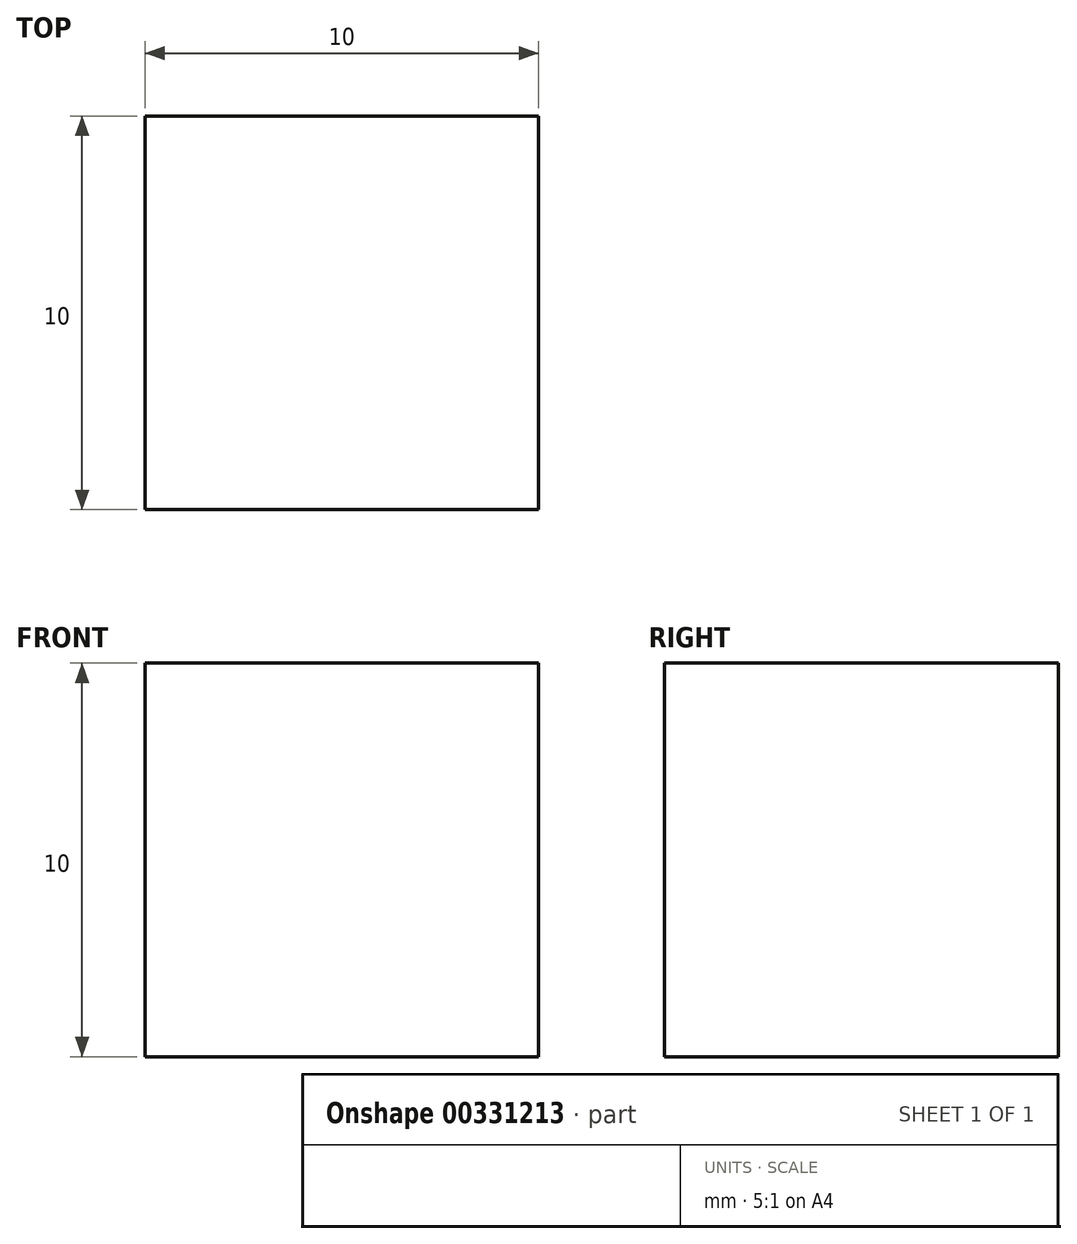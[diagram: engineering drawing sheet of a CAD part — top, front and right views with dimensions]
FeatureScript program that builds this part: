
annotation { "Feature Type Name" : "Feature", "Feature Type Description" : "" }
export const myFeature = defineFeature(function(context is Context, id is Id, definition is map)
    precondition{}
    {
        {
            var Q0;
            Q0=qCreatedBy(makeId("Front.planeOp"),FACE);
            var sketch = newSketch(context, id + "F0", { "sketchPlane" : qUnion([Q0])});
            skLineSegment(sketch, "E0.bottom", {"start": v(5, -5) * mm, "end": v(-5, -5) * mm});
            skLineSegment(sketch, "E0.top", {"start": v(5, 5) * mm, "end": v(-5, 5) * mm});
            skLineSegment(sketch, "E0.left", {"start": v(5, -5) * mm, "end": v(5, 5) * mm});
            skLineSegment(sketch, "E0.right", {"start": v(-5, -5) * mm, "end": v(-5, 5) * mm});
            skPoint(sketch, "E0.middle", {"position": v(0, 0) * mm});
            skSolve(sketch);
        }
        {
            var Q0;
            Q0 = qSketchRegion(id + "F0", true);
            extrude(context, id + "F1", {"entities" : qUnion([Q0]), "depth" : 10 * mm});
        }
    });
